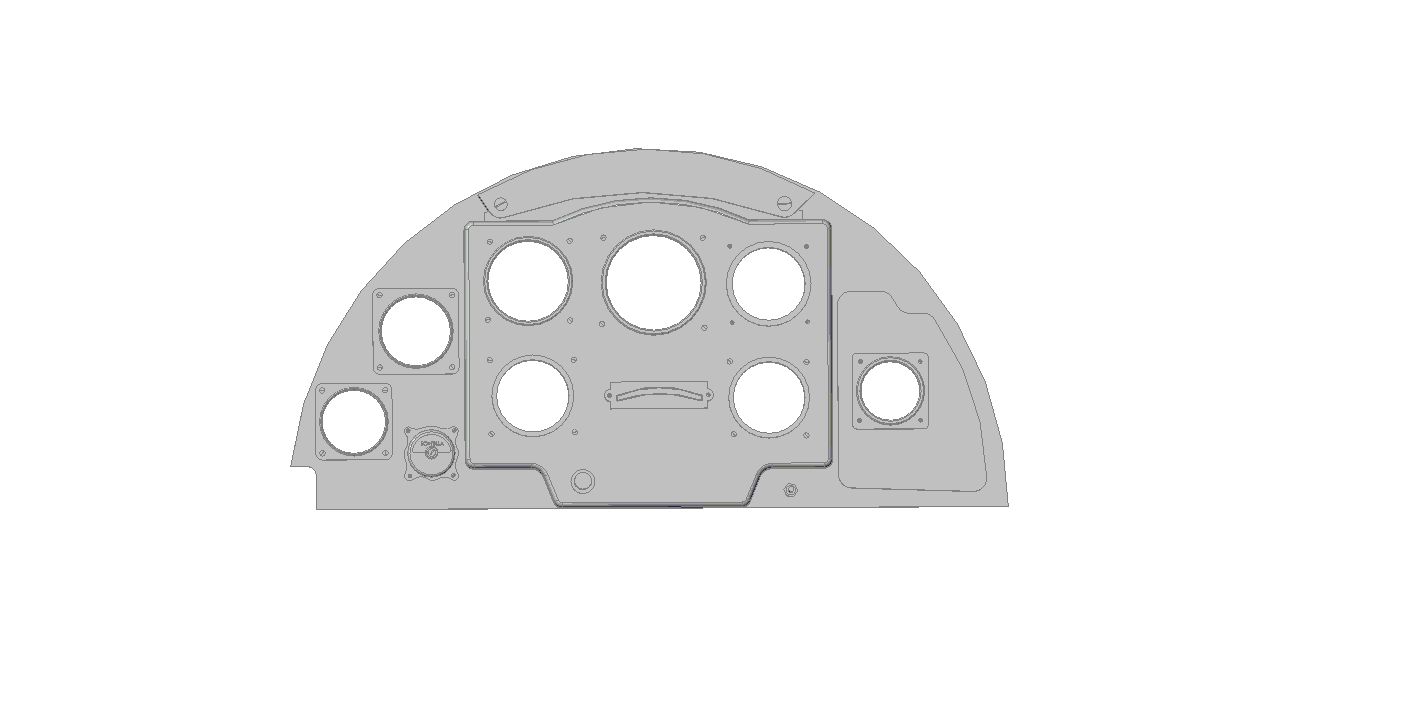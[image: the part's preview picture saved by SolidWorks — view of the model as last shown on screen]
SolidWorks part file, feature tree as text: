
SOLIDWORKS PART (.sldprt)
format: sldprt  version: not decoded by parser v0  size: 3,234,304 bytes
history: native  units: mm
features: sketch x156, cut_extrude x99, fillet x75, extrude x45, plane x3, mirror x2, material x1 (+8 scaffold rows collapsed)
feature tree (389):
  scaffold x8  (default folders/planes/origin — collapsed)
  material  "Matériau <non spécifié>"
  plane  "Plan de face"
  plane  "Plan de dessus"
  plane  "Plan de droite"
  sketch  "Esquisse1"  dims[c1.D1=80.0mm c1.D4=80.0mm c1.D2=168.0mm c1.D3=~80.158811mm c2.D1=80.4mm c2.D2=80.0mm c2.D3=80.4mm]
  extrude  "Extrusion1"  Depth=0.8mm
  sketch  "Esquisse2"
  extrude  "Extrusion2"  Depth=5mm
  fillet  "Congé1"  Radius=2mm
  fillet  "Congé2"  Radius=2mm
  sketch  "Esquisse3"  dims[D1=5.0mm D5=10.0mm D6=10.0mm D7=5.0mm]
  sketch  "Esquisse4"
  cut_extrude  "Enlèv. mat.-Extru.1"  Depth=5mm
  sketch  "Esquisse5"  dims[D1=~16.696445mm]
  cut_extrude  "Enlèv. mat.-Extru.2"  Depth=5mm
  fillet  "Congé3"  Radius=2mm
  fillet  "Congé4"  Radius=3mm
  fillet  "Congé5"  Radius=2mm
  fillet  "Congé6"  Radius=1mm
  sketch  "Esquisse6"
  extrude  "Extrusion3"  Depth=4mm
  sketch  "Esquisse7"  dims[D1=7.0mm]
  extrude  "Extrusion4"  Depth=5.5mm
  fillet  "Congé7"  Radius=3mm
  fillet  "Congé8"  Radius=3mm
  sketch  "Esquisse8"
  extrude  "Extrusion5"  Depth=0.3mm
  mirror  "Symétrie1"
  sketch  "Esquisse9"  dims[D1=~2.841949mm]
  extrude  "Extrusion6"  Depth=0.3mm
  sketch  "Esquisse13"
  cut_extrude  "Enlèv. mat.-Extru.14"  Depth=0.2mm
  sketch  "Esquisse14"
  cut_extrude  "Enlèv. mat.-Extru.15"  Depth=0.2mm
  sketch  "Esquisse15"
  extrude  "Extrusion7"  Depth=0.4mm
  sketch  "Esquisse20"
  extrude  "Extrusion8"  Depth=0.5mm
  sketch  "Esquisse22"
  cut_extrude  "Enlèv. mat.-Extru.16"  [1 undecoded]
  fillet  "Congé9"  Radius=1.5mm
  fillet  "Congé10"  Radius=1.5mm
  fillet  "Congé11"  Radius=1.5mm
  fillet  "Congé12"  Radius=1.5mm
  sketch  "Esquisse23"
  cut_extrude  "Enlèv. mat.-Extru.17"  Depth=0.2mm
  sketch  "Esquisse24"  dims[D1=1.2mm]
  cut_extrude  "Enlèv. mat.-Extru.18"  Depth=0.2mm
  sketch  "Esquisse25"
  cut_extrude  "Enlèv. mat.-Extru.19"  Depth=0.2mm
  sketch  "Esquisse26"
  cut_extrude  "Enlèv. mat.-Extru.20"  Depth=0.2mm
  sketch  "Esquisse27"  dims[D1=1.2mm]
  cut_extrude  "Enlèv. mat.-Extru.21"  Depth=0.2mm
  sketch  "Esquisse28"
  cut_extrude  "Enlèv. mat.-Extru.22"  Depth=0.2mm
  sketch  "Esquisse29"
  cut_extrude  "Enlèv. mat.-Extru.23"  Depth=0.2mm
  sketch  "Esquisse30"
  cut_extrude  "Enlèv. mat.-Extru.24"  Depth=0.2mm
  sketch  "Esquisse31"
  cut_extrude  "Enlèv. mat.-Extru.25"  [1 undecoded]
  sketch  "Esquisse32"
  cut_extrude  "Enlèv. mat.-Extru.26"  [1 undecoded]
  sketch  "Esquisse33"
  extrude  "Extrusion9"  Depth=0.4mm
  fillet  "Congé13"  Radius=1.5mm
  fillet  "Congé14"  Radius=1.5mm
  fillet  "Congé15"  Radius=1.5mm
  fillet  "Congé16"  Radius=1.5mm
  sketch  "Esquisse35"
  extrude  "Extrusion10"  Depth=0.5mm
  sketch  "Esquisse36"
  cut_extrude  "Enlèv. mat.-Extru.27"  [1 undecoded]
  sketch  "Esquisse37"
  cut_extrude  "Enlèv. mat.-Extru.28"  Depth=0.2mm
  sketch  "Esquisse38"
  cut_extrude  "Enlèv. mat.-Extru.29"  Depth=0.2mm
  sketch  "Esquisse39"
  cut_extrude  "Enlèv. mat.-Extru.30"  Depth=0.2mm
  sketch  "Esquisse40"
  cut_extrude  "Enlèv. mat.-Extru.31"  Depth=0.2mm
  fillet  "Congé17"  Radius=0.25mm
  fillet  "Congé18"  Radius=0.25mm
  fillet  "Congé19"  Radius=0.25mm
  fillet  "Congé20"  Radius=0.25mm
  sketch  "Esquisse41"
  cut_extrude  "Enlèv. mat.-Extru.32"  Depth=0.2mm
  sketch  "Esquisse42"
  cut_extrude  "Enlèv. mat.-Extru.33"  Depth=0.2mm
  sketch  "Esquisse43"
  cut_extrude  "Enlèv. mat.-Extru.34"  Depth=0.2mm
  sketch  "Esquisse44"
  cut_extrude  "Enlèv. mat.-Extru.35"  Depth=0.2mm
  sketch  "Esquisse48"
  extrude  "Extrusion12"  Depth=0.2mm
  sketch  "Esquisse49"
  cut_extrude  "Enlèv. mat.-Extru.38"  Depth=0.2mm
  sketch  "Esquisse50"
  cut_extrude  "Enlèv. mat.-Extru.39"  Depth=0.2mm
  sketch  "Esquisse51"
  cut_extrude  "Enlèv. mat.-Extru.40"  Depth=0.2mm
  sketch  "Esquisse52"
  cut_extrude  "Enlèv. mat.-Extru.41"  Depth=0.2mm
  mirror  "Symétrie11"
  sketch  "Esquisse56"
  cut_extrude  "Enlèv. mat.-Extru.44"  Depth=0.2mm
  fillet  "Congé25"  Radius=1mm
  fillet  "Congé26"  Radius=1mm
  fillet  "Congé27"  Radius=1mm
  fillet  "Congé28"  Radius=1mm
  fillet  "Congé29"  Radius=1mm
  fillet  "Congé35"  Radius=2mm
  fillet  "Congé37"  Radius=2mm
  fillet  "Congé40"  Radius=2mm
  fillet  "Congé41"  Radius=2mm
  fillet  "Congé42"  Radius=2mm
  sketch  "Esquisse58"
  cut_extrude  "Enlèv. mat.-Extru.46"  Depth=0.2mm
  fillet  "Congé47"  Radius=3mm
  fillet  "Congé48"  Radius=3mm
  fillet  "Congé49"  Radius=3mm
  fillet  "Congé50"  Radius=3mm
  sketch  "Esquisse59"
  cut_extrude  "Enlèv. mat.-Extru.47"  Depth=0.2mm
  fillet  "Congé51"  Radius=3mm
  fillet  "Congé52"  Radius=3mm
  sketch  "Esquisse60"
  cut_extrude  "Enlèv. mat.-Extru.48"  Depth=0.2mm
  fillet  "Congé53"  Radius=3mm
  fillet  "Congé54"  Radius=3mm
  sketch  "Esquisse61"
  extrude  "Extrusion13"  Depth=1mm
  fillet  "Congé55"  Radius=0.5mm
  sketch  "Esquisse62"
  cut_extrude  "Enlèv. mat.-Extru.49"  Depth=0.3mm
  fillet  "Congé56"  Radius=0.5mm
  fillet  "Congé57"  Radius=0.5mm
  sketch  "Esquisse64"
  extrude  "Extrusion15"  Depth=0.5mm
  fillet  "Congé59"  Radius=0.2mm
  sketch  "Esquisse65"
  extrude  "Extrusion16"  Depth=0.1mm
  fillet  "Congé60"  Radius=0.05mm
  sketch  "Esquisse66"
  cut_extrude  "Enlèv. mat.-Extru.50"  Depth=0.5mm
  sketch  "Esquisse67"
  cut_extrude  "Enlèv. mat.-Extru.51"  Depth=0.1mm
  sketch  "Esquisse68"  dims[D1=~0.894999mm]
  extrude  "Extrusion18"  Depth=0.2mm
  fillet  "Congé61"  Radius=0.1mm
  sketch  "Esquisse69"
  cut_extrude  "Enlèv. mat.-Extru.52"  Depth=0.2mm
  sketch  "Esquisse70"
  extrude  "Extrusion19"  Depth=0.8mm
  sketch  "Esquisse71"
  extrude  "Extrusion20"  Depth=0.2mm
  sketch  "Esquisse72"
  extrude  "Extrusion21"  Depth=6mm
  sketch  "Esquisse76"  dims[D1=20.0mm]
  extrude  "Extrusion22"  Depth=0.5mm
  sketch  "Esquisse77"
  cut_extrude  "Enlèv. mat.-Extru.53"  [1 undecoded]
  fillet  "Congé62"  Radius=0.25mm
  fillet  "Congé63"  Radius=0.25mm
  sketch  "Esquisse78"
  extrude  "Extrusion23"  Depth=1mm
  sketch  "Esquisse79"
  extrude  "Extrusion24"  Depth=1mm
  sketch  "Esquisse80"
  extrude  "Extrusion25"  Depth=1mm
  sketch  "Esquisse81"
  extrude  "Extrusion26"  Depth=1mm
  sketch  "Esquisse82"
  extrude  "Extrusion27"  Depth=1mm
  sketch  "Esquisse83"
  sketch  "Esquisse84"
  cut_extrude  "Enlèv. mat.-Extru.54"  [1 undecoded]
  sketch  "Esquisse85"
  sketch  "Esquisse86"
  cut_extrude  "Enlèv. mat.-Extru.55"  [1 undecoded]
  sketch  "Esquisse87"
  cut_extrude  "Enlèv. mat.-Extru.56"  [1 undecoded]
  sketch  "Esquisse89"
  cut_extrude  "Enlèv. mat.-Extru.58"  [1 undecoded]
  fillet  "Congé64"  Radius=0.25mm
  sketch  "Esquisse90"
  sketch  "Esquisse92"
  extrude  "Extrusion30"  Depth=1mm
  fillet  "Congé66"  Radius=3mm
  fillet  "Congé67"  Radius=3mm
  fillet  "Congé68"  Radius=3mm
  fillet  "Congé69"  Radius=3mm
  fillet  "Congé70"  Radius=3mm
  fillet  "Congé71"  Radius=3mm
  sketch  "Esquisse93"
  extrude  "Extrusion31"  Depth=0.8mm
  fillet  "Congé72"  Radius=1mm
  fillet  "Congé73"  Radius=1mm
  fillet  "Congé74"  Radius=1mm
  fillet  "Congé75"  Radius=1mm
  sketch  "Esquisse94"
  extrude  "Extrusion32"  Depth=2mm
  sketch  "Esquisse95"
  cut_extrude  "Enlèv. mat.-Extru.60"  [1 undecoded]
  fillet  "Congé76"  Radius=0.25mm
  sketch  "Esquisse96"
  extrude  "Extrusion33"  Depth=0.5mm
  sketch  "Esquisse97"
  extrude  "Extrusion34"  Depth=3mm
  sketch  "Esquisse98"
  cut_extrude  "Enlèv. mat.-Extru.61"  Depth=3mm
  sketch  "Esquisse100"
  cut_extrude  "Enlèv. mat.-Extru.62"  Depth=3mm
  sketch  "Esquisse101"
  sketch  "Esquisse102"
  cut_extrude  "Enlèv. mat.-Extru.63"  Depth=3mm
  sketch  "Esquisse103"
  cut_extrude  "Enlèv. mat.-Extru.64"  Depth=3mm
  sketch  "Esquisse104"  dims[D1=~0.894999mm]
  extrude  "Extrusion35"  Depth=0.2mm
  fillet  "Congé78"  Radius=0.1mm
  sketch  "Esquisse106"
  cut_extrude  "Enlèv. mat.-Extru.66"  Depth=0.2mm
  sketch  "Esquisse107"
  cut_extrude  "Enlèv. mat.-Extru.67"  Depth=0.2mm
  sketch  "Esquisse108"
  cut_extrude  "Enlèv. mat.-Extru.68"  Depth=0.2mm
  sketch  "1"  dims[D1=1.2mm]
  sketch  "3"  dims[D1=1.2mm]
  cut_extrude  "Enlèv. mat.-Extru.71"  Depth=0.2mm
  sketch  "4"
  cut_extrude  "Enlèv. mat.-Extru.72"  Depth=0.2mm
  sketch  "5"
  cut_extrude  "Enlèv. mat.-Extru.73"  Depth=0.2mm
  sketch  "6"
  cut_extrude  "Enlèv. mat.-Extru.74"  Depth=0.2mm
  sketch  "7"
  cut_extrude  "Enlèv. mat.-Extru.75"  Depth=0.2mm
  sketch  "8"
  cut_extrude  "Enlèv. mat.-Extru.76"  Depth=0.2mm
  sketch  "9"
  cut_extrude  "Enlèv. mat.-Extru.77"  Depth=0.2mm
  sketch  "10"
  cut_extrude  "Enlèv. mat.-Extru.78"  Depth=0.2mm
  sketch  "11"
  cut_extrude  "Enlèv. mat.-Extru.79"  Depth=0.2mm
  sketch  "12"
  cut_extrude  "Enlèv. mat.-Extru.80"  Depth=0.2mm
  sketch  "13"  dims[D1=1.2mm]
  cut_extrude  "Enlèv. mat.-Extru.81"  Depth=0.2mm
  sketch  "14"
  cut_extrude  "Enlèv. mat.-Extru.82"  Depth=0.2mm
  sketch  "Esquisse117"
  cut_extrude  "Enlèv. mat.-Extru.83"  Depth=4.2mm
  sketch  "Esquisse118"
  sketch  "Esquisse119"
  sketch  "Esquisse120"
  cut_extrude  "Enlèv. mat.-Extru.86"  Depth=4.2mm
  sketch  "Esquisse121"
  cut_extrude  "Enlèv. mat.-Extru.87"  Depth=4.2mm
  sketch  "Esquisse122"  dims[D1=14.0mm]
  sketch  "15"  dims[D1=1.2mm]
  cut_extrude  "Enlèv. mat.-Extru.88"  Depth=0.2mm
  sketch  "16"
  cut_extrude  "Enlèv. mat.-Extru.89"  Depth=0.2mm
  sketch  "19"  dims[D1=~0.894999mm]
  extrude  "Extrusion37"  Depth=0.2mm
  sketch  "Esquisse135"
  fillet  "Congé80"  Radius=0.1mm
  sketch  "20"
  cut_extrude  "Enlèv. mat.-Extru.91"  Depth=0.2mm
  sketch  "21"  dims[D1=~0.894999mm]
  extrude  "Extrusion38"  Depth=0.2mm
  fillet  "Congé81"  Radius=0.1mm
  sketch  "22"
  cut_extrude  "Enlèv. mat.-Extru.92"  Depth=0.2mm
  sketch  "23"  dims[D1=~0.894999mm]
  extrude  "Extrusion39"  Depth=0.2mm
  fillet  "Congé82"  Radius=0.1mm
  sketch  "24"
  cut_extrude  "Enlèv. mat.-Extru.93"  Depth=0.2mm
  sketch  "25"  dims[D1=~0.894999mm]
  extrude  "Extrusion40"  Depth=0.2mm
  fillet  "Congé83"  Radius=0.1mm
  sketch  "26"
  cut_extrude  "Enlèv. mat.-Extru.94"  Depth=0.2mm
  sketch  "27"  dims[D1=~0.894999mm]
  extrude  "Extrusion41"  Depth=0.2mm
  fillet  "Congé84"  Radius=0.1mm
  sketch  "28"
  cut_extrude  "Enlèv. mat.-Extru.95"  Depth=0.2mm
  sketch  "29"  dims[D1=~0.894999mm]
  extrude  "Extrusion42"  Depth=0.2mm
  fillet  "Congé85"  Radius=0.1mm
  sketch  "30"
  cut_extrude  "Enlèv. mat.-Extru.96"  Depth=0.2mm
  sketch  "31"  dims[D1=1.2mm]
  cut_extrude  "Enlèv. mat.-Extru.97"  Depth=0.2mm
  sketch  "32"
  cut_extrude  "Enlèv. mat.-Extru.98"  Depth=0.2mm
  sketch  "33"
  cut_extrude  "Enlèv. mat.-Extru.99"  Depth=0.2mm
  sketch  "34"
  cut_extrude  "Enlèv. mat.-Extru.100"  Depth=0.2mm
  sketch  "35"
  cut_extrude  "Enlèv. mat.-Extru.101"  Depth=0.2mm
  sketch  "36"
  cut_extrude  "Enlèv. mat.-Extru.102"  Depth=0.2mm
  sketch  "37"
  cut_extrude  "Enlèv. mat.-Extru.103"  Depth=0.2mm
  sketch  "38"
  cut_extrude  "Enlèv. mat.-Extru.104"  Depth=0.2mm
  sketch  "Esquisse161"
  sketch  "47"
  cut_extrude  "Enlèv. mat.-Extru.110"  Depth=0.2mm
  sketch  "48"
  cut_extrude  "Enlèv. mat.-Extru.111"  Depth=0.2mm
  sketch  "49"
  cut_extrude  "Enlèv. mat.-Extru.112"  Depth=0.2mm
  sketch  "50"
  cut_extrude  "Enlèv. mat.-Extru.113"  Depth=0.2mm
  sketch  "51"
  cut_extrude  "Enlèv. mat.-Extru.114"  Depth=0.2mm
  sketch  "52"
  cut_extrude  "Enlèv. mat.-Extru.115"  Depth=0.2mm
  sketch  "53"
  cut_extrude  "Enlèv. mat.-Extru.116"  Depth=0.2mm
  sketch  "54"
  cut_extrude  "Enlèv. mat.-Extru.117"  Depth=0.2mm
  sketch  "55"  dims[D1=~0.894999mm]
  extrude  "Extrusion48"  Depth=0.2mm
  fillet  "Congé92"  Radius=0.1mm
  sketch  "56"
  cut_extrude  "Enlèv. mat.-Extru.118"  Depth=0.2mm
  sketch  "57"  dims[D1=~0.894999mm]
  extrude  "Extrusion49"  Depth=0.2mm
  fillet  "Congé93"  Radius=0.1mm
  sketch  "58"
  cut_extrude  "Enlèv. mat.-Extru.119"  Depth=0.2mm
  sketch  "59"  dims[D1=~0.894999mm]
  extrude  "Extrusion50"  Depth=0.2mm
  fillet  "Congé94"  Radius=0.1mm
  sketch  "60"
  cut_extrude  "Enlèv. mat.-Extru.120"  Depth=0.2mm
  sketch  "61"  dims[D1=~0.894999mm]
  extrude  "Extrusion51"  Depth=0.2mm
  fillet  "Congé95"  Radius=0.1mm
  sketch  "62"
  cut_extrude  "Enlèv. mat.-Extru.121"  Depth=0.2mm
  sketch  "Esquisse187"
  cut_extrude  "Enlèv. mat.-Extru.122"  Depth=4mm
  sketch  "Esquisse188"
  cut_extrude  "Enlèv. mat.-Extru.123"  Depth=4mm
  sketch  "Esquisse189"
  cut_extrude  "Enlèv. mat.-Extru.124"  Depth=4mm
  sketch  "Esquisse190"  dims[D1=15.0mm]
  cut_extrude  "Enlèv. mat.-Extru.125"  Depth=2mm
  sketch  "Esquisse191"
  sketch  "Esquisse192"
  extrude  "Extrusion53"  Depth=2.5mm
  sketch  "Esquisse193"
  extrude  "Extrusion54"  Depth=2.5mm
  sketch  "Esquisse194"
  extrude  "Extrusion55"  Depth=2.5mm
  sketch  "Esquisse195"
  cut_extrude  "Enlèv. mat.-Extru.126"  Depth=1mm
  fillet  "Congé97"  Radius=0.2mm
  fillet  "Congé98"  Radius=0.2mm
  fillet  "Congé99"  Radius=0.2mm
  fillet  "Congé100"  Radius=0.2mm
  sketch  "63"  dims[D1=~0.894999mm]
  extrude  "Extrusion56"  Depth=0.2mm
  fillet  "Congé101"  Radius=0.1mm
  sketch  "64"
  cut_extrude  "Enlèv. mat.-Extru.127"  Depth=0.2mm
  sketch  "65"  dims[D1=~0.894999mm]
  extrude  "Extrusion57"  Depth=0.2mm
  fillet  "Congé102"  Radius=0.1mm
  sketch  "66"
  cut_extrude  "Enlèv. mat.-Extru.128"  Depth=0.2mm
decode coverage: 238 of 377 modeling features carry decoded parameters
note: ~ marks probable driven/reference dimensions
note: 10 parameter values undecoded
summary: no parameter record found for 10 features
note: suppression state not decoded; provenance and decode notes live in map.json
